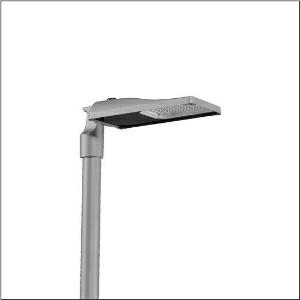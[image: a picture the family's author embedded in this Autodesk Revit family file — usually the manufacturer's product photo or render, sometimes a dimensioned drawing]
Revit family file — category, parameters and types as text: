
# Revit family: streetlight_sl_31_mini___st1_0a_5xh2d3as08ha_8082
name_source: partatom
category: Lighting Fixtures
units: mm (PartAtom-declared; Revit-internal decimal feet)

## family parameters
Cut with Voids When Loaded = No
Host = Face
Light Source = No
Part Type = Normal
Room Calculation Point = No
Round Connector Dimension = Use Diameter
Shared = No

## types (1)
- --- (1 x LED, 9230 lm, 68.3 W, 3000K)
    Apparent Load = 68 VA
    CIE Flux Codes = 37 72 97 100 100
    Color Rendering = 70
    Color Temperature = 3000K
    Default Elevation = 1800 mm
    Description = Streetlight SL 31 mini D4i mast luminaire for post-top, side-entry; light control with lens of PMMA; light distribution: ST1.0a, direct asymmetric distribution, for standard-compliant lighting for roads and squares; LED: luminous flux: 9.230lm, light colour: 730, colour temperature: 3000K; luminous efficacy: 135,1lm/W; control: pre-setting: logarithmic dimming characteristic, flexible luminous flux parameterisation, time-dependent luminous flux control, constant luminous flux control, power reduction, intelligent temperature release in ECG and LED module, overheat protection; luminaire housing, of diecast aluminium, Siteco® metallic grey (DB 702S), corrosivity category C5 high according to DIN EN ISO 12944; cover of toughened safety glass, transparent, mast flange of diecast aluminium, Siteco® metallic grey (DB 702S), spigot size: 76/60mm, mast flange included unmounted; with cable H07RN-F 2x 1.5mm², cable length: 8,5m, connection cable pre-assembled; mains connection: 220..240V, AC, 50/60Hz; power consumption (at start of service life): 68,3W / (at end of service life): 74,5W / (with reduced operation 50%): 29,5W; protection rating (complete): IP66; insulation class (complete): insulation class II (safety insulation); impact resistance: IK10; certification: CE, ENEC, ENEC+, VDE, UKCA, ZD4i; permissible operating ambient temperature for outdoor applications: -40..+50°C; packaging unit: 1 piece

Light Distribution: ST1.0a
    Height = 76 mm
    Lamp = 1 x LED
    Lamp Light Flux = 9230 lm
    Lamp Power = 68.3 W
    Lamp count = 1
    Length = 547 mm
    Luminous efficacy = 135 lm/W
    Manufacturer = Siteco
    ModVariant = No
    Model = 5XH2D3AS08HA
    Number of Poles = 1
    OnlyDefault = Yes
    Power Factor = 1
    Product Name = Streetlight SL 31 mini | ST1.0a
    Product group = mast luminaire | pylon top
    ProductGroupID = 6100
    Protection Class = Protection class II
    Protection Degree = IP 66
    RLX_Detail_Level = 1
    RLX_Emergency_Light_Flux = 0 lm
    RLX_Emergency_Type = 0
    RLX_Emergency_Type_DB = No
    RlxData = <blob elided: 39305 chars, md5=02cd14b2>
    Socket = socket
    Standby Power = 0 W
    System Light Flux = 9230 lm
    System Power = 68 W
    Type Comments = factory setting: luminous flux: 100 % | dim-lin: 254 | 692 mA
    Type Image = l_1300330.jpg
    URL = http://relux.com
    VarID = @adj_019531
    Voltage = 0 V
    Weight = 0.00 kg
    Width = 265 mm

## geometry (parser evidence)
native form markers: Blend x4, Sweep x9
no freeform markers — native parametric forms only
